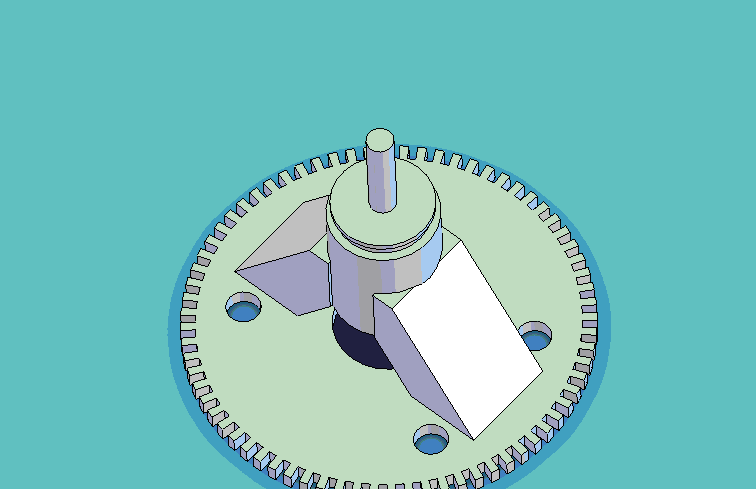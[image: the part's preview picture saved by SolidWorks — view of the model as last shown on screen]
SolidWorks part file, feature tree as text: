
SOLIDWORKS PART (.sldprt)
format: sldprt  version: not decoded by parser v0  size: 947,200 bytes
history: native  units: mm
features: sketch x15, cut_extrude x7, extrude x6, plane x3, material x1, pattern_linear x1, pattern_circular x1 (+10 scaffold rows collapsed)
feature tree (44):
  scaffold x10  (default folders/planes/origin — collapsed)
  material  "Material <not specified>"
  plane  "Frontal"
  plane  "Horizontal"
  plane  "Profile"
  sketch  "Sketch1"  dims[D1=149.352mm]
  extrude  "Extrude1"  Depth=6.35mm
  sketch  "Sketch2"  dims[D1=38.1mm D2=112.776mm]
  extrude  "Extrude2"  Depth=50.8mm
  sketch  "Sketch3"  dims[c1.D1=22.352mm c1.D2=22.352mm c2.D2=54.0deg c2.D3=22.352mm c3.D3=54.0deg c3.D4=53.594mm]
  cut_extrude  "Cut-Extrude2"  [1 undecoded]
  sketch  "Sketch4"  dims[c1.D1=~56.960543mm c2.D1=54.0deg c2.D2=~64.776803mm c3.D2=54.0deg]
  cut_extrude  "Cut-Extrude3"  Depth=50.8mm
  sketch  "Sketch5"
  cut_extrude  "Cut-Extrude4"  Depth=50.8mm
  sketch  "Sketch6"  dims[D1=~37.281016mm]
  extrude  "Extrude3"  Depth=50.546mm
  sketch  "Sketch7"  dims[D1=~26.401626mm]
  cut_extrude  "Cut-Extrude5"  [1 undecoded]
  sketch  "Sketch8"  dims[D1=~10.384366mm]
  extrude  "Extrude4"  Depth=4.826mm
  sketch  "Sketch9"  dims[D1=~27.14099mm]
  extrude  "Extrude5"  Depth=2.286mm
  sketch  "Sketch10"  dims[D1=~6.957439mm]
  extrude  "Extrude6"  Depth=40.64mm
  sketch  "Sketch11"  dims[D1=44.196mm D2=28.448mm]
  cut_extrude  "Cut-Extrude6"  Depth=20.32mm
  sketch  "Sketch12"
  pattern_linear  "LPattern1"  Count1=2 Count2=2 Spacing1=88.392mm Spacing2=56.896mm
  sketch  "Sketch16"  dims[c1.D1=~111.382153mm c2.D1=2.5deg]
  cut_extrude  "Cut-Extrude8"  Depth=20.32mm
  sketch  "Sketch18"  dims[c1.D1=~82.973333mm c2.D1=2.5deg c2.D2=~85.315029mm c3.D2=2.5deg]
  cut_extrude  "Cut-Extrude9"  Depth=20.32mm
  sketch  "Sketch19"
  pattern_circular  "CirPattern1"  Count=72 Angle=360deg
decode coverage: 25 of 30 modeling features carry decoded parameters
note: ~ marks probable driven/reference dimensions
note: 2 parameter values undecoded
note: suppression state not decoded; provenance and decode notes live in map.json
